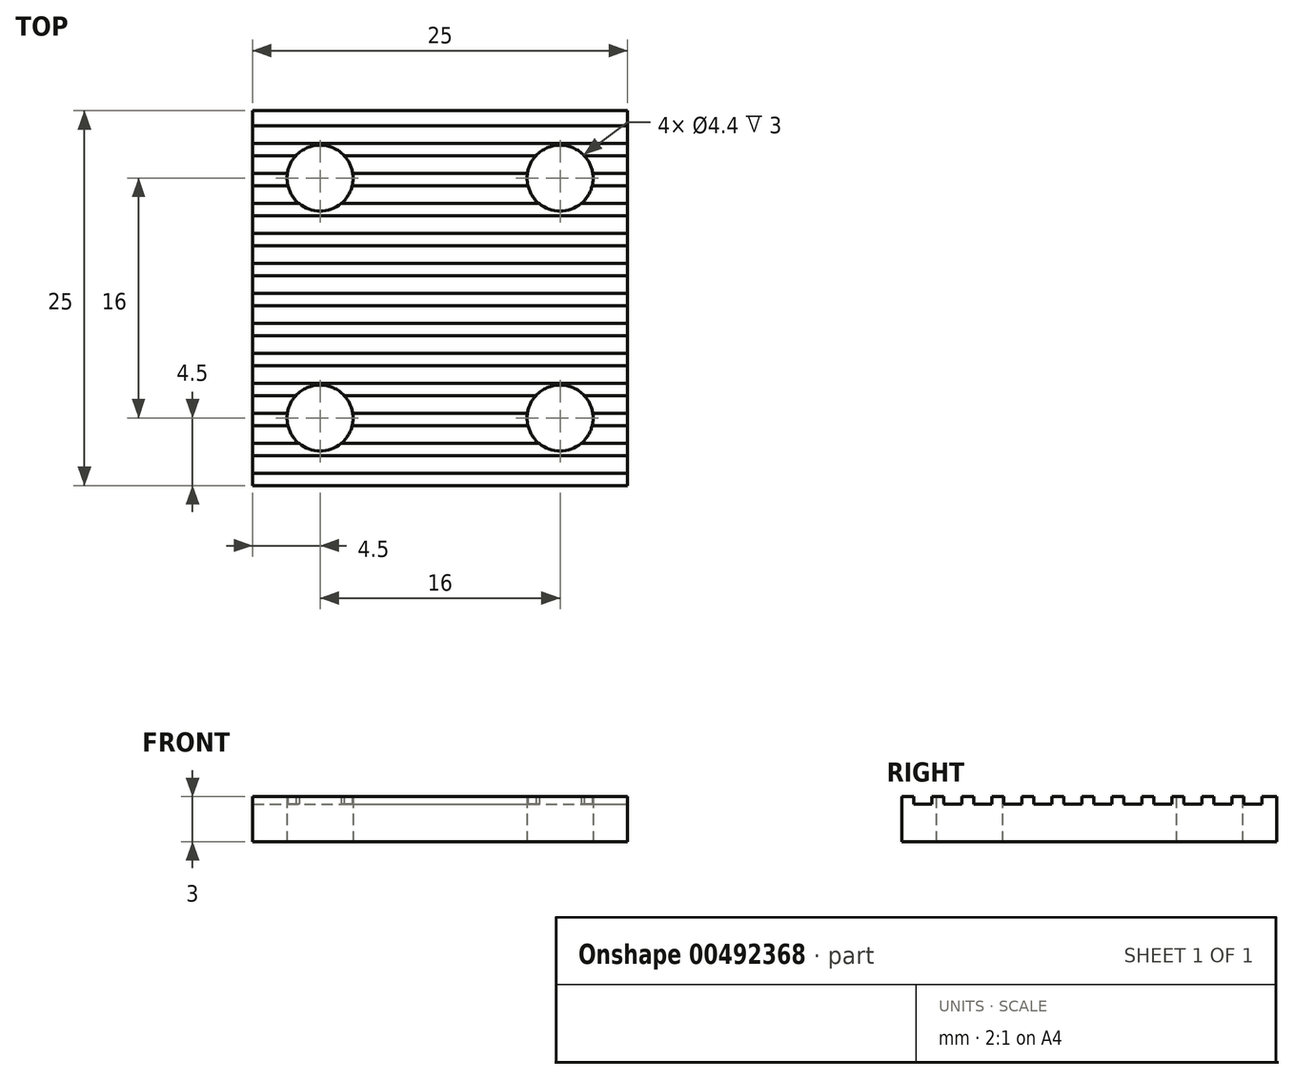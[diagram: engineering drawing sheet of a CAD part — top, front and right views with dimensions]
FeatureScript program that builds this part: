
annotation { "Feature Type Name" : "Feature", "Feature Type Description" : "" }
export const myFeature = defineFeature(function(context is Context, id is Id, definition is map)
    precondition{}
    {
        {
            var Q0;
            Q0=qCreatedBy(makeId("Top.planeOp"),FACE);
            var sketch = newSketch(context, id + "F0", { "sketchPlane" : qUnion([Q0])});
            skLineSegment(sketch, "E0.bottom", {"start": v(-12.5, -12.5) * mm, "end": v(12.5, -12.5) * mm});
            skLineSegment(sketch, "E0.top", {"start": v(-12.5, 12.5) * mm, "end": v(12.5, 12.5) * mm});
            skLineSegment(sketch, "E0.left", {"start": v(-12.5, -12.5) * mm, "end": v(-12.5, 12.5) * mm});
            skLineSegment(sketch, "E0.right", {"start": v(12.5, -12.5) * mm, "end": v(12.5, 12.5) * mm});
            skPoint(sketch, "E1", {"position": v(-8, 8) * mm});
            skPoint(sketch, "E2", {"position": v(8, -8) * mm});
            skPoint(sketch, "E3", {"position": v(8, 8) * mm});
            skPoint(sketch, "E4", {"position": v(-8, -8) * mm});
            skSolve(sketch);
        }
        {
            var Q0;
            Q0 = qSketchRegion(id + "F0", true);
            extrude(context, id + "F1", {"entities" : qUnion([Q0]), "depth" : 3 * mm});
        }
        {
            var Q0;
            Q0=sQuery(id+"F0.wireOp",VERTEX,"E1");
            var Q1;
            Q1=sQuery(id+"F0.wireOp",VERTEX,"E3");
            var Q2;
            Q2=sQuery(id+"F0.wireOp",VERTEX,"E2");
            var Q3;
            Q3=sQuery(id+"F0.wireOp",VERTEX,"E4");
            var Q4;
            Q4=makeQuery(id+"F1.opExtrude","SWEPT_BODY",BODY,{"disambiguationData":[OSD([sQuery(id+"F0.wireOp",EDGE,"E0.bottom"),sQuery(id+"F0.wireOp",EDGE,"E0.top"),sQuery(id+"F0.wireOp",EDGE,"E0.left"),sQuery(id+"F0.wireOp",EDGE,"E0.right")])]});
            hole(context, id + "F2", {"style" : HoleStyle.SIMPLE, "endStyle" : HoleEndStyle.THROUGH, "oppositeDirection" : true, "standardTappedOrClearance" : lookupTablePath({ "standard" : "ISO", "fit" : "Normal", "size" : "M4", "type" : "Clearance" }), "standardBlindInLast" : lookupTablePath({ "fit" : "Standard", "standard" : "ISO", "size" : "M4", "type" : "Clearance" }), "holeDiameter" : 4.4 * mm, "isTappedThrough" : true, "tappedDepth" : 12 * mm, "tapClearance" : 3, "locations" : qUnion([Q0, Q1, Q2, Q3]), "scope" : qUnion([Q4])});
        }
        {
            var Q0;
            Q0=makeQuery(id+"F1.opExtrude","SWEPT_FACE",FACE,{"disambiguationData":[OSD([sQuery(id+"F0.wireOp",EDGE,"E0.right")])]});
            var sketch = newSketch(context, id + "F3", { "sketchPlane" : qUnion([Q0])});
            skLineSegment(sketch, "E5.bottom", {"start": v(-11.7, 3) * mm, "end": v(-10.5, 3) * mm});
            skLineSegment(sketch, "E5.top", {"start": v(-11.7, 2.5) * mm, "end": v(-10.5, 2.5) * mm});
            skLineSegment(sketch, "E5.left", {"start": v(-11.7, 3) * mm, "end": v(-11.7, 2.5) * mm});
            skLineSegment(sketch, "E5.right", {"start": v(-10.5, 3) * mm, "end": v(-10.5, 2.5) * mm});
            skLineSegment(sketch, "E6.1.0.0", {"start": v(-8.5, 3) * mm, "end": v(-8.5, 2.5) * mm});
            skLineSegment(sketch, "E6.1.0.1", {"start": v(-9.7, 3) * mm, "end": v(-8.5, 3) * mm});
            skLineSegment(sketch, "E6.1.0.2", {"start": v(-9.7, 3) * mm, "end": v(-9.7, 2.5) * mm});
            skLineSegment(sketch, "E6.1.0.3", {"start": v(-9.7, 2.5) * mm, "end": v(-8.5, 2.5) * mm});
            skLineSegment(sketch, "E6.2.0.0", {"start": v(-6.5, 3) * mm, "end": v(-6.5, 2.5) * mm});
            skLineSegment(sketch, "E6.2.0.1", {"start": v(-7.7, 3) * mm, "end": v(-6.5, 3) * mm});
            skLineSegment(sketch, "E6.2.0.2", {"start": v(-7.7, 3) * mm, "end": v(-7.7, 2.5) * mm});
            skLineSegment(sketch, "E6.2.0.3", {"start": v(-7.7, 2.5) * mm, "end": v(-6.5, 2.5) * mm});
            skLineSegment(sketch, "E6.3.0.0", {"start": v(-4.5, 3) * mm, "end": v(-4.5, 2.5) * mm});
            skLineSegment(sketch, "E6.3.0.1", {"start": v(-5.7, 3) * mm, "end": v(-4.5, 3) * mm});
            skLineSegment(sketch, "E6.3.0.2", {"start": v(-5.7, 3) * mm, "end": v(-5.7, 2.5) * mm});
            skLineSegment(sketch, "E6.3.0.3", {"start": v(-5.7, 2.5) * mm, "end": v(-4.5, 2.5) * mm});
            skLineSegment(sketch, "E6.4.0.0", {"start": v(-2.5, 3) * mm, "end": v(-2.5, 2.5) * mm});
            skLineSegment(sketch, "E6.4.0.1", {"start": v(-3.7, 3) * mm, "end": v(-2.5, 3) * mm});
            skLineSegment(sketch, "E6.4.0.2", {"start": v(-3.7, 3) * mm, "end": v(-3.7, 2.5) * mm});
            skLineSegment(sketch, "E6.4.0.3", {"start": v(-3.7, 2.5) * mm, "end": v(-2.5, 2.5) * mm});
            skLineSegment(sketch, "E6.5.0.0", {"start": v(-0.5, 3) * mm, "end": v(-0.5, 2.5) * mm});
            skLineSegment(sketch, "E6.5.0.1", {"start": v(-1.7, 3) * mm, "end": v(-0.5, 3) * mm});
            skLineSegment(sketch, "E6.5.0.2", {"start": v(-1.7, 3) * mm, "end": v(-1.7, 2.5) * mm});
            skLineSegment(sketch, "E6.5.0.3", {"start": v(-1.7, 2.5) * mm, "end": v(-0.5, 2.5) * mm});
            skLineSegment(sketch, "E6.6.0.0", {"start": v(1.5, 3) * mm, "end": v(1.5, 2.5) * mm});
            skLineSegment(sketch, "E6.6.0.1", {"start": v(0.3, 3) * mm, "end": v(1.5, 3) * mm});
            skLineSegment(sketch, "E6.6.0.2", {"start": v(0.3, 3) * mm, "end": v(0.3, 2.5) * mm});
            skLineSegment(sketch, "E6.6.0.3", {"start": v(0.3, 2.5) * mm, "end": v(1.5, 2.5) * mm});
            skLineSegment(sketch, "E6.7.0.0", {"start": v(3.5, 3) * mm, "end": v(3.5, 2.5) * mm});
            skLineSegment(sketch, "E6.7.0.1", {"start": v(2.3, 3) * mm, "end": v(3.5, 3) * mm});
            skLineSegment(sketch, "E6.7.0.2", {"start": v(2.3, 3) * mm, "end": v(2.3, 2.5) * mm});
            skLineSegment(sketch, "E6.7.0.3", {"start": v(2.3, 2.5) * mm, "end": v(3.5, 2.5) * mm});
            skLineSegment(sketch, "E6.8.0.0", {"start": v(5.5, 3) * mm, "end": v(5.5, 2.5) * mm});
            skLineSegment(sketch, "E6.8.0.1", {"start": v(4.3, 3) * mm, "end": v(5.5, 3) * mm});
            skLineSegment(sketch, "E6.8.0.2", {"start": v(4.3, 3) * mm, "end": v(4.3, 2.5) * mm});
            skLineSegment(sketch, "E6.8.0.3", {"start": v(4.3, 2.5) * mm, "end": v(5.5, 2.5) * mm});
            skLineSegment(sketch, "E6.9.0.0", {"start": v(7.5, 3) * mm, "end": v(7.5, 2.5) * mm});
            skLineSegment(sketch, "E6.9.0.1", {"start": v(6.3, 3) * mm, "end": v(7.5, 3) * mm});
            skLineSegment(sketch, "E6.9.0.2", {"start": v(6.3, 3) * mm, "end": v(6.3, 2.5) * mm});
            skLineSegment(sketch, "E6.9.0.3", {"start": v(6.3, 2.5) * mm, "end": v(7.5, 2.5) * mm});
            skLineSegment(sketch, "E6.10.0.0", {"start": v(9.5, 3) * mm, "end": v(9.5, 2.5) * mm});
            skLineSegment(sketch, "E6.10.0.1", {"start": v(8.3, 3) * mm, "end": v(9.5, 3) * mm});
            skLineSegment(sketch, "E6.10.0.2", {"start": v(8.3, 3) * mm, "end": v(8.3, 2.5) * mm});
            skLineSegment(sketch, "E6.10.0.3", {"start": v(8.3, 2.5) * mm, "end": v(9.5, 2.5) * mm});
            skLineSegment(sketch, "E6.11.0.0", {"start": v(11.5, 3) * mm, "end": v(11.5, 2.5) * mm});
            skLineSegment(sketch, "E6.11.0.1", {"start": v(10.3, 3) * mm, "end": v(11.5, 3) * mm});
            skLineSegment(sketch, "E6.11.0.2", {"start": v(10.3, 3) * mm, "end": v(10.3, 2.5) * mm});
            skLineSegment(sketch, "E6.11.0.3", {"start": v(10.3, 2.5) * mm, "end": v(11.5, 2.5) * mm});
            skLineSegment(sketch, "E6.direction1", {"start": v(-10.5, 2.5) * mm, "end": v(-8.5, 2.5) * mm, "construction": true});
            skSolve(sketch);
        }
        {
            var Q0;
            Q0 = qSketchRegion(id + "F3", true);
            extrude(context, id + "F4", {"entities" : qUnion([Q0]), "operationType" : NewBodyOperationType.REMOVE, "endBound" : BoundingType.THROUGH_ALL, "oppositeDirection" : true, "depth" : 25 * mm});
        }
    });
